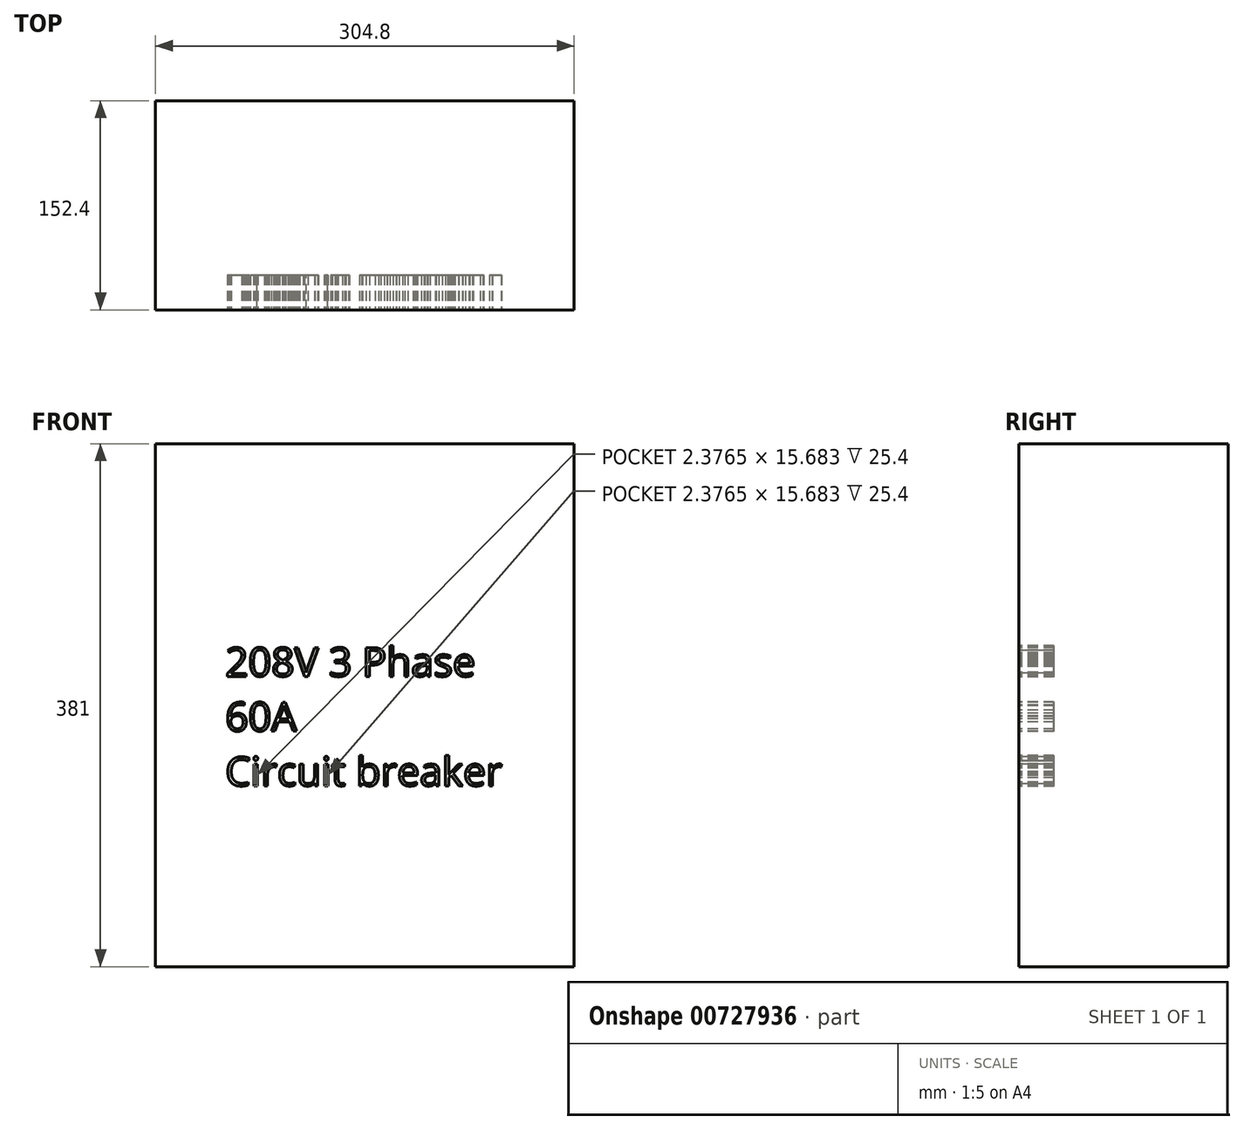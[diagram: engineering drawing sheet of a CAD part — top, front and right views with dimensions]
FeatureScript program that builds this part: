
annotation { "Feature Type Name" : "Feature", "Feature Type Description" : "" }
export const myFeature = defineFeature(function(context is Context, id is Id, definition is map)
    precondition{}
    {
        {
            var Q0;
            Q0=qCreatedBy(makeId("Front.planeOp"),FACE);
            var sketch = newSketch(context, id + "F0", { "sketchPlane" : qUnion([Q0])});
            skLineSegment(sketch, "E0.bottom", {"start": v(152.4, -190.5) * mm, "end": v(-152.4, -190.5) * mm});
            skLineSegment(sketch, "E0.top", {"start": v(152.4, 190.5) * mm, "end": v(-152.4, 190.5) * mm});
            skLineSegment(sketch, "E0.left", {"start": v(152.4, -190.5) * mm, "end": v(152.4, 190.5) * mm});
            skLineSegment(sketch, "E0.right", {"start": v(-152.4, -190.5) * mm, "end": v(-152.4, 190.5) * mm});
            skPoint(sketch, "E0.middle", {"position": v(0, 0) * mm});
            skSolve(sketch);
        }
        {
            var Q0;
            Q0 = qSketchRegion(id + "F0", true);
            extrude(context, id + "F1", {"entities" : qUnion([Q0]), "depth" : 152.4 * mm, "offsetDistance" : 25.4 * mm});
        }
        {
            var Q0;
            Q0=makeQuery(id+"F1.opExtrude","CAP_FACE",FACE,{"disambiguationData":[OSD([sQuery(id+"F0.wireOp",EDGE,"E0.bottom"),sQuery(id+"F0.wireOp",EDGE,"E0.top"),sQuery(id+"F0.wireOp",EDGE,"E0.left"),sQuery(id+"F0.wireOp",EDGE,"E0.right")])],"isStart":false});
            var sketch = newSketch(context, id + "F2", { "sketchPlane" : qUnion([Q0])});
            skText(sketch, "E1", { "text": "208V 3 Phase\n60A\nCircuit breaker\n", "fontName": "OpenSans-Regular.ttf"});
            const initialGuessF2  = {"E1": [-0.1016, 0.02095, 1, 0, 0.0211]};
            skSetInitialGuess(sketch, initialGuessF2);
            skSolve(sketch);
        }
        {
            var Q0;
            Q0 = qSketchRegion(id + "F2", true);
            extrude(context, id + "F3", {"entities" : qUnion([Q0]), "operationType" : NewBodyOperationType.REMOVE, "oppositeDirection" : true, "depth" : 25.4 * mm, "offsetDistance" : 25.4 * mm});
        }
    });
